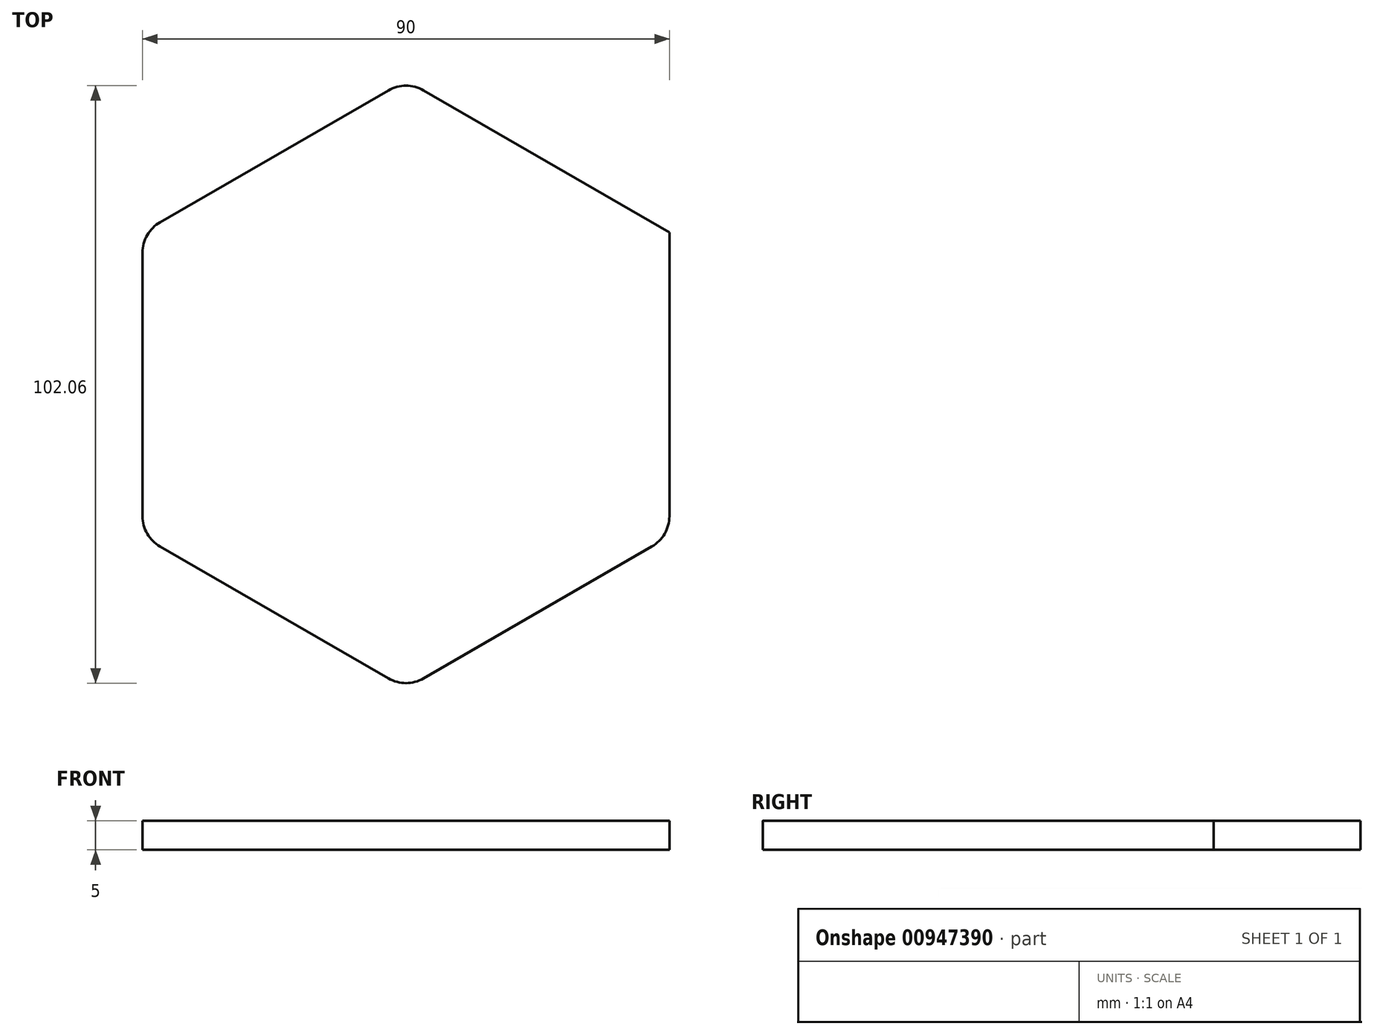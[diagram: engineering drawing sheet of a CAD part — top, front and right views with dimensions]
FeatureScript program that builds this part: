
annotation { "Feature Type Name" : "Feature", "Feature Type Description" : "" }
export const myFeature = defineFeature(function(context is Context, id is Id, definition is map)
    precondition{}
    {
        {
            var Q0;
            Q0=qCreatedBy(makeId("Top.planeOp"),FACE);
            var sketch = newSketch(context, id + "F0", { "sketchPlane" : qUnion([Q0])});
            skCircle(sketch, "E0.cCircle", {"center": v(0, 0) * mm, "radius": 51.96 * mm, "construction": true});
            skLineSegment(sketch, "E0.0", {"start": v(3, 50.23) * mm, "end": v(45, 25.98) * mm});
            skLineSegment(sketch, "E0.1", {"start": v(45, 25.98) * mm, "end": v(45, -22.52) * mm});
            skLineSegment(sketch, "E0.2", {"start": v(42, -27.71) * mm, "end": v(3, -50.23) * mm});
            skLineSegment(sketch, "E0.3", {"start": v(-3, -50.23) * mm, "end": v(-42, -27.71) * mm});
            skLineSegment(sketch, "E0.4", {"start": v(-45, -22.52) * mm, "end": v(-45, 22.52) * mm});
            skLineSegment(sketch, "E0.5", {"start": v(-42, 27.71) * mm, "end": v(-3, 50.23) * mm});
            skPoint(sketch, "E1.visualSharp", {"position": v(0, 51.96) * mm});
            skArc(sketch, "E1.filletArc", {"start": v(3, 50.23) * mm, "mid": v(0, 51.03) * mm, "end": v(-3, 50.23) * mm});
            skPoint(sketch, "E2.visualSharp", {"position": v(-45, 25.98) * mm});
            skArc(sketch, "E2.filletArc", {"start": v(-42, 27.71) * mm, "mid": v(-44.2, 25.52) * mm, "end": v(-45, 22.52) * mm});
            skPoint(sketch, "E3.visualSharp", {"position": v(-45, -25.98) * mm});
            skArc(sketch, "E3.filletArc", {"start": v(-45, -22.52) * mm, "mid": v(-44.2, -25.52) * mm, "end": v(-42, -27.71) * mm});
            skPoint(sketch, "E4.visualSharp", {"position": v(0, -51.96) * mm});
            skArc(sketch, "E4.filletArc", {"start": v(-3, -50.23) * mm, "mid": v(0, -51.03) * mm, "end": v(3, -50.23) * mm});
            skPoint(sketch, "E5.visualSharp", {"position": v(45, -25.98) * mm});
            skArc(sketch, "E5.filletArc", {"start": v(42, -27.71) * mm, "mid": v(44.2, -25.52) * mm, "end": v(45, -22.52) * mm});
            skSolve(sketch);
        }
        {
            var Q0;
            Q0=makeQuery(id+"F0.imprint","IMPRINT",FACE,{"disambiguationData":[TD([[makeQuery(id+"F0.imprint","IMPRINT",EDGE,{"derivedFrom":sQuery(id+"F0.wireOp",EDGE,"E0.0")}),-1.0]])]});
            extrude(context, id + "F1", {"entities" : qUnion([Q0]), "depth" : 5 * mm, "offsetDistance" : 25 * mm});
        }
    });
